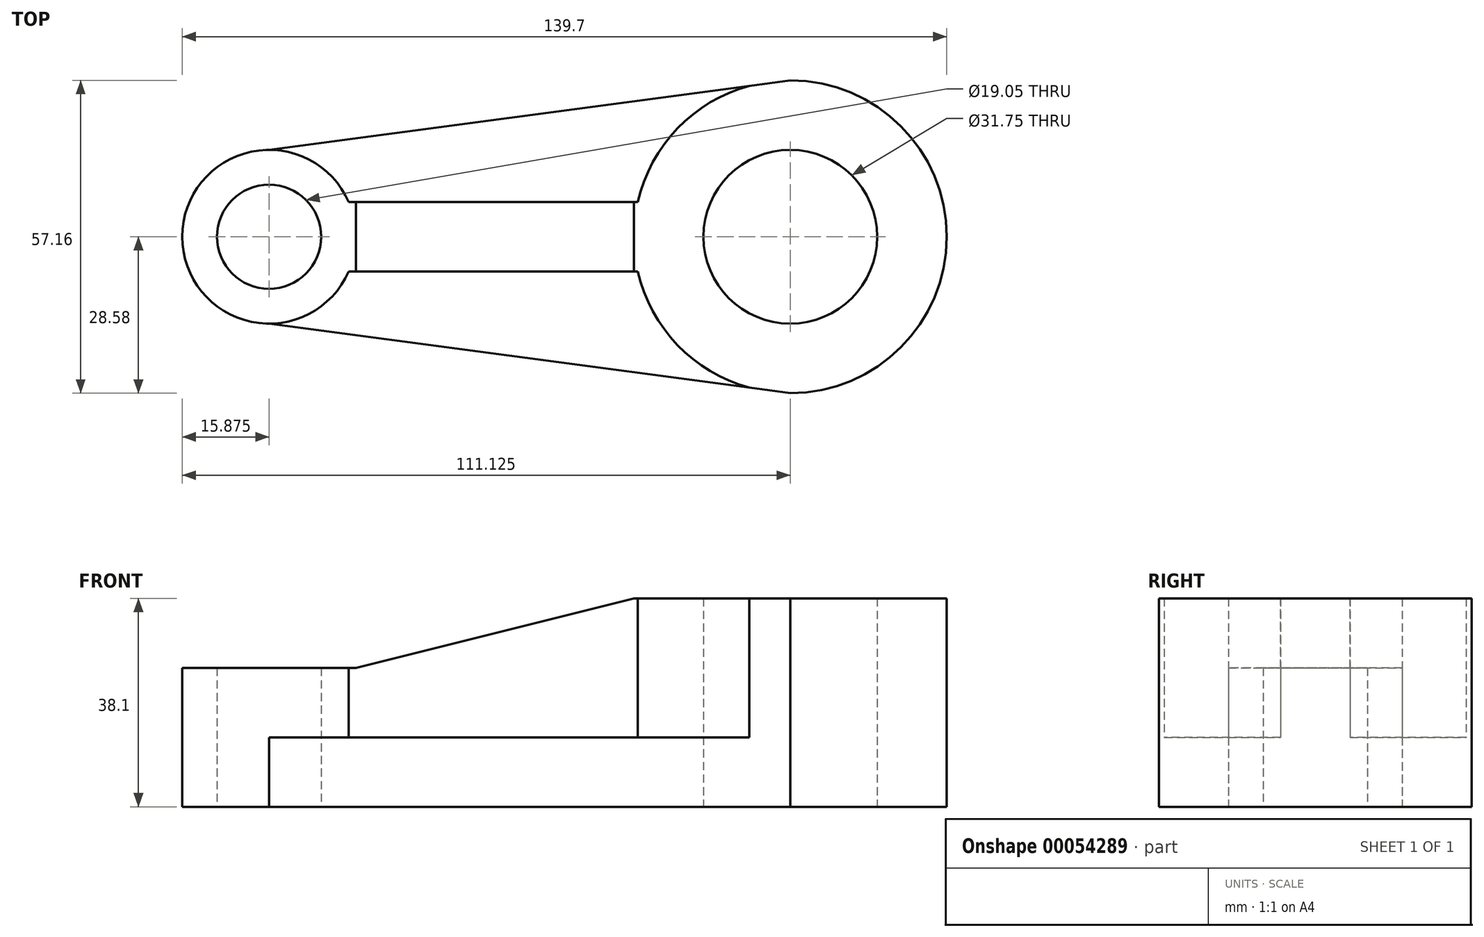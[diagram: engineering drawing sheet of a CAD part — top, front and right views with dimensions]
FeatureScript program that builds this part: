
annotation { "Feature Type Name" : "Feature", "Feature Type Description" : "" }
export const myFeature = defineFeature(function(context is Context, id is Id, definition is map)
    precondition{}
    {
        {
            var Q0;
            Q0=qCreatedBy(makeId("Top.planeOp"),FACE);
            var sketch = newSketch(context, id + "F0", { "sketchPlane" : qUnion([Q0])});
            skCircle(sketch, "E0", {"center": v(28.57, 0) * mm, "radius": 15.88 * mm});
            skCircle(sketch, "E1", {"center": v(28.57, 0) * mm, "radius": 28.58 * mm});
            skCircle(sketch, "E2", {"center": v(-66.68, 0) * mm, "radius": 9.53 * mm});
            skCircle(sketch, "E3", {"center": v(-66.68, 0) * mm, "radius": 15.88 * mm});
            skLineSegment(sketch, "E4", {"start": v(-66.68, 15.87) * mm, "end": v(28.57, 28.58) * mm});
            skLineSegment(sketch, "E5", {"start": v(28.57, 28.58) * mm, "end": v(28.57, -28.58) * mm});
            skLineSegment(sketch, "E6", {"start": v(28.57, -28.58) * mm, "end": v(-66.68, -15.88) * mm});
            skLineSegment(sketch, "E7", {"start": v(-66.68, -15.88) * mm, "end": v(-66.68, 15.88) * mm});
            skSolve(sketch);
        }
        {
            var Q0;
            {var subQ0=sQuery(id+"F0.wireOp",EDGE,"E7");var subQ1=sQuery(id+"F0.wireOp",EDGE,"E2");var subQ2=makeQuery(id+"F0.imprint","INTERSECT",VERTEX,{"disambiguationData":[OD(0.0)],"derivedFrom":[subQ1,subQ0]});Q0=makeQuery(id+"F0.imprint","IMPRINT",FACE,{"disambiguationData":[TD([[makeQuery(id+"F0.imprint","IMPRINT",EDGE,{"disambiguationData":[TD([[subQ2,1.0]])],"derivedFrom":subQ1}),-1.0]])]});}
            var Q1;
            {var subQ0=sQuery(id+"F0.wireOp",EDGE,"E7");var subQ1=sQuery(id+"F0.wireOp",EDGE,"E2");var subQ2=makeQuery(id+"F0.imprint","INTERSECT",VERTEX,{"disambiguationData":[OD(0.0)],"derivedFrom":[subQ1,subQ0]});Q1=makeQuery(id+"F0.imprint","IMPRINT",FACE,{"disambiguationData":[TD([[makeQuery(id+"F0.imprint","IMPRINT",EDGE,{"disambiguationData":[TD([[subQ2,-1.0]])],"derivedFrom":subQ1}),-1.0]])]});}
            var Q2;
            Q2=sQuery(id+"F0.wireOp",EDGE,"E2");
            var Q3;
            Q3=sQuery(id+"F0.wireOp",EDGE,"E3");
            extrude(context, id + "F1", {"entities" : qUnion([Q0, Q1]), "surfaceEntities" : qUnion([Q2, Q3]), "depth" : 25.4 * mm});
        }
        {
            var Q0;
            {var subQ0=sQuery(id+"F0.wireOp",EDGE,"E5");var subQ4=sQuery(id+"F0.wireOp",EDGE,"E0");var subQ5=makeQuery(id+"F0.imprint","INTERSECT",VERTEX,{"disambiguationData":[OD(0.0)],"derivedFrom":[subQ4,subQ0]});Q0=makeQuery(id+"F0.imprint","IMPRINT",FACE,{"disambiguationData":[TD([[makeQuery(id+"F0.imprint","IMPRINT",EDGE,{"disambiguationData":[TD([[subQ5,-1.0]])],"derivedFrom":subQ4}),-1.0]])]});}
            var Q1;
            {var subQ0=sQuery(id+"F0.wireOp",EDGE,"E5");var subQ1=sQuery(id+"F0.wireOp",EDGE,"E0");var subQ2=makeQuery(id+"F0.imprint","INTERSECT",VERTEX,{"disambiguationData":[OD(0.0)],"derivedFrom":[subQ1,subQ0]});Q1=makeQuery(id+"F0.imprint","IMPRINT",FACE,{"disambiguationData":[TD([[makeQuery(id+"F0.imprint","IMPRINT",EDGE,{"disambiguationData":[TD([[subQ2,1.0]])],"derivedFrom":subQ1}),-1.0]])]});}
            extrude(context, id + "F2", {"entities" : qUnion([Q0, Q1]), "depth" : 38.1 * mm});
        }
        {
            var Q0;
            {var subQ0=sQuery(id+"F0.wireOp",EDGE,"E4");var subQ1=sQuery(id+"F0.wireOp",EDGE,"E1");var subQ2=makeQuery(id+"F0.imprint","INTERSECT",VERTEX,{"derivedFrom":[subQ1,subQ0]});Q0=makeQuery(id+"F0.imprint","IMPRINT",FACE,{"disambiguationData":[TD([[makeQuery(id+"F0.imprint","IMPRINT",EDGE,{"disambiguationData":[TD([[subQ2,-1.0]])],"derivedFrom":subQ1}),-1.0]])]});}
            extrude(context, id + "F3", {"entities" : qUnion([Q0]), "operationType" : NewBodyOperationType.ADD, "depth" : 12.7 * mm});
        }
        {
            var Q0;
            Q0=qCreatedBy(makeId("Front.planeOp"),FACE);
            var sketch = newSketch(context, id + "F4", { "sketchPlane" : qUnion([Q0])});
            skLineSegment(sketch, "E8", {"start": v(0, 0) * mm, "end": v(-50.8, 0) * mm});
            skLineSegment(sketch, "E9", {"start": v(-50.8, 0) * mm, "end": v(-50.8, 25.4) * mm, "construction": true});
            skLineSegment(sketch, "E10", {"start": v(-50.8, 25.4) * mm, "end": v(0, 38.1) * mm});
            skLineSegment(sketch, "E11", {"start": v(0, 38.1) * mm, "end": v(0, 0) * mm, "construction": true});
            skLineSegment(sketch, "E12", {"start": v(-50.8, 0) * mm, "end": v(-54.5, 0) * mm});
            skLineSegment(sketch, "E13", {"start": v(-54.5, 0) * mm, "end": v(-54.5, 25.4) * mm});
            skLineSegment(sketch, "E14", {"start": v(-54.5, 25.4) * mm, "end": v(-50.8, 25.4) * mm});
            skLineSegment(sketch, "E15", {"start": v(0, 0) * mm, "end": v(4.62, 0) * mm});
            skLineSegment(sketch, "E16", {"start": v(4.62, 0) * mm, "end": v(4.62, 38.1) * mm});
            skLineSegment(sketch, "E17", {"start": v(4.62, 38.1) * mm, "end": v(0, 38.1) * mm});
            skSolve(sketch);
        }
        {
            var Q0;
            Q0=makeQuery(id+"F4.imprint","IMPRINT",FACE,{"disambiguationData":[TD([[makeQuery(id+"F4.imprint","IMPRINT",EDGE,{"derivedFrom":sQuery(id+"F4.wireOp",EDGE,"E8")}),-1.0]])]});
            extrude(context, id + "F5", {"entities" : qUnion([Q0]), "operationType" : NewBodyOperationType.ADD, "endBound" : BoundingType.SYMMETRIC, "depth" : 12.7 * mm});
        }
    });
